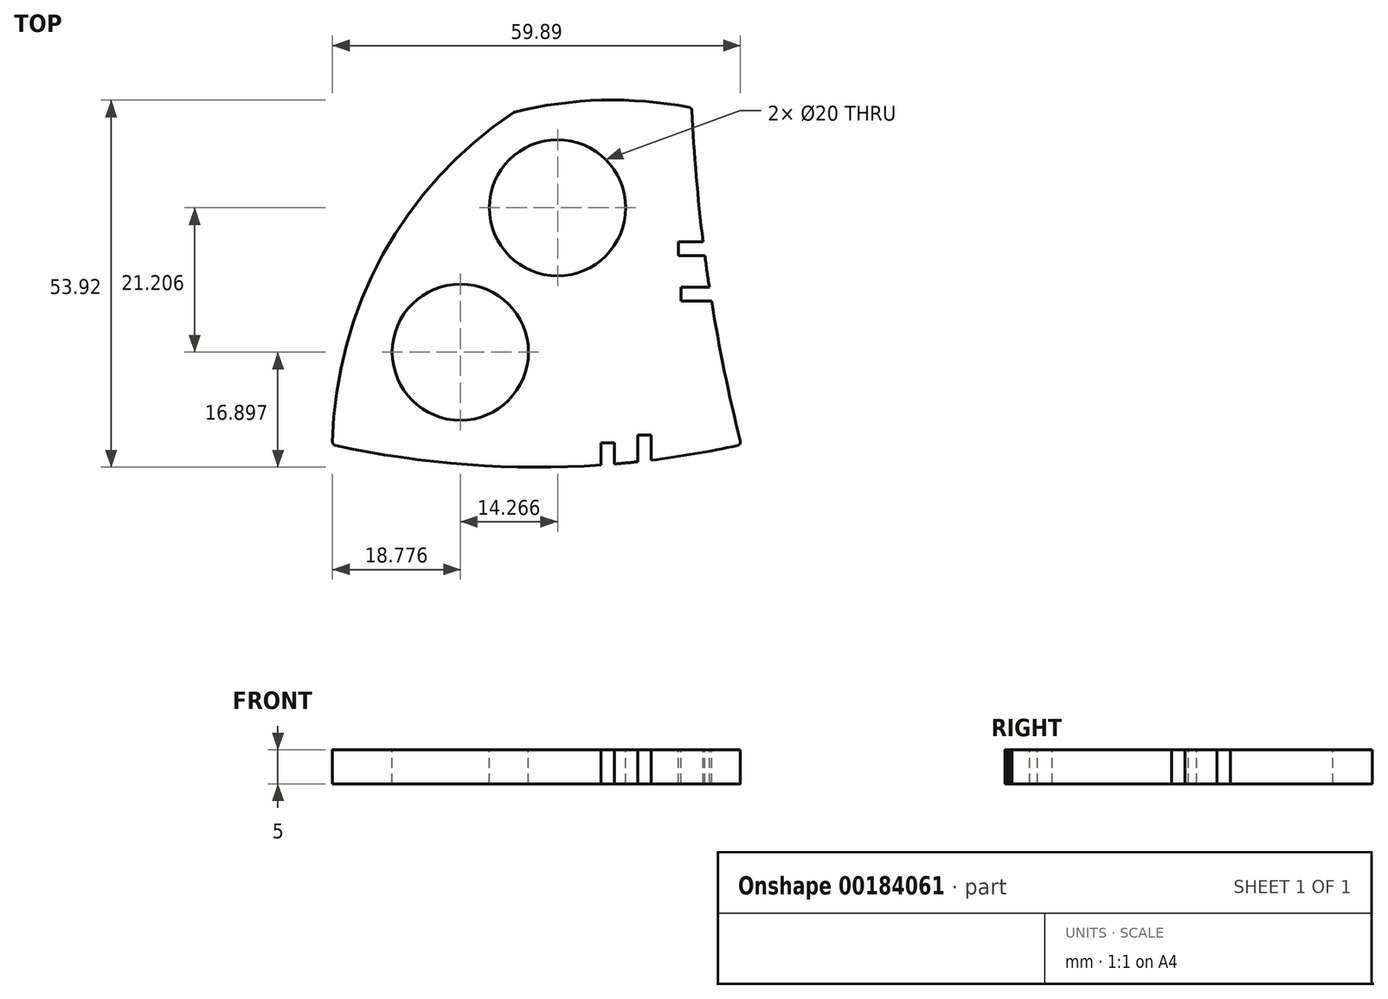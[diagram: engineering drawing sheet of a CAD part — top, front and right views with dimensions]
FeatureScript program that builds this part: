
annotation { "Feature Type Name" : "Feature", "Feature Type Description" : "" }
export const myFeature = defineFeature(function(context is Context, id is Id, definition is map)
    precondition{}
    {
        {
            var Q0;
            Q0=qCreatedBy(makeId("Top.planeOp"),FACE);
            var sketch = newSketch(context, id + "F0", { "sketchPlane" : qUnion([Q0])});
            skArc(sketch, "E0", {"start": v(-12.1, 38.1) * mm, "mid": v(-25.17, 39.22) * mm, "end": v(-38.18, 37.48) * mm});
            skArc(sketch, "E1", {"start": v(-12.1, 38.1) * mm, "mid": v(-9.74, 13.18) * mm, "end": v(-4.85, -11.37) * mm});
            skArc(sketch, "E2", {"start": v(-64.85, -11.37) * mm, "mid": v(-34.85, -14.68) * mm, "end": v(-4.85, -11.37) * mm});
            skArc(sketch, "E3", {"start": v(-38.18, 37.48) * mm, "mid": v(-57.55, 16.35) * mm, "end": v(-64.85, -11.37) * mm});
            skSolve(sketch);
        }
        {
            var Q0;
            Q0=makeQuery(id+"F0.imprint","IMPRINT",FACE,{"disambiguationData":[TD([[makeQuery(id+"F0.imprint","IMPRINT",EDGE,{"derivedFrom":sQuery(id+"F0.wireOp",EDGE,"E0")}),1.0]])]});
            extrude(context, id + "F1", {"entities" : qUnion([Q0]), "depth" : 5 * mm});
        }
        {
            var Q0;
            Q0=makeQuery(id+"F1.opExtrude","CAP_FACE",FACE,{"disambiguationData":[OSD([sQuery(id+"F0.wireOp",EDGE,"E0"),sQuery(id+"F0.wireOp",EDGE,"E1"),sQuery(id+"F0.wireOp",EDGE,"E2"),sQuery(id+"F0.wireOp",EDGE,"E3")])],"isStart":false});
            var sketch = newSketch(context, id + "F2", { "sketchPlane" : qUnion([Q0])});
            skLineSegment(sketch, "E4.bottom", {"start": v(-14.07, 18.41) * mm, "end": v(16.42, 18.41) * mm});
            skLineSegment(sketch, "E4.top", {"start": v(-14.07, 16.41) * mm, "end": v(16.42, 16.41) * mm});
            skLineSegment(sketch, "E4.left", {"start": v(-14.07, 18.41) * mm, "end": v(-14.07, 16.41) * mm});
            skLineSegment(sketch, "E4.right", {"start": v(16.42, 18.41) * mm, "end": v(16.42, 16.41) * mm});
            skLineSegment(sketch, "E5.bottom", {"start": v(-13.69, 11.74) * mm, "end": v(37.06, 11.74) * mm});
            skLineSegment(sketch, "E5.top", {"start": v(-13.69, 9.74) * mm, "end": v(37.06, 9.74) * mm});
            skLineSegment(sketch, "E5.left", {"start": v(-13.69, 11.74) * mm, "end": v(-13.69, 9.74) * mm});
            skLineSegment(sketch, "E5.right", {"start": v(37.06, 11.74) * mm, "end": v(37.06, 9.74) * mm});
            skLineSegment(sketch, "E6.bottom", {"start": v(-20.05, -21.1) * mm, "end": v(-18.05, -21.1) * mm});
            skLineSegment(sketch, "E6.top", {"start": v(-20.05, -9.93) * mm, "end": v(-18.05, -9.93) * mm});
            skLineSegment(sketch, "E6.left", {"start": v(-20.05, -21.1) * mm, "end": v(-20.05, -9.93) * mm});
            skLineSegment(sketch, "E6.right", {"start": v(-18.05, -21.1) * mm, "end": v(-18.05, -9.93) * mm});
            skLineSegment(sketch, "E7.bottom", {"start": v(-25.45, -11.08) * mm, "end": v(-23.45, -11.08) * mm});
            skLineSegment(sketch, "E7.top", {"start": v(-25.45, -26.31) * mm, "end": v(-23.45, -26.31) * mm});
            skLineSegment(sketch, "E7.left", {"start": v(-25.45, -11.08) * mm, "end": v(-25.45, -26.31) * mm});
            skLineSegment(sketch, "E7.right", {"start": v(-23.45, -11.08) * mm, "end": v(-23.45, -26.31) * mm});
            skSolve(sketch);
        }
        {
            var Q0;
            {var subQ0=sQuery(id+"F2.wireOp",EDGE,"E4.left");Q0=makeQuery(id+"F2.imprint","IMPRINT",FACE,{"disambiguationData":[TD([[makeQuery(id+"F2.imprint","IMPRINT",EDGE,{"derivedFrom":subQ0}),1.0]])]});}
            var Q1;
            {var subQ0=sQuery(id+"F2.wireOp",EDGE,"E5.left");Q1=makeQuery(id+"F2.imprint","IMPRINT",FACE,{"disambiguationData":[TD([[makeQuery(id+"F2.imprint","IMPRINT",EDGE,{"derivedFrom":subQ0}),1.0]])]});}
            var Q2;
            {var subQ0=sQuery(id+"F2.wireOp",EDGE,"E7.bottom");Q2=makeQuery(id+"F2.imprint","IMPRINT",FACE,{"disambiguationData":[TD([[makeQuery(id+"F2.imprint","IMPRINT",EDGE,{"derivedFrom":subQ0}),-1.0]])]});}
            var Q3;
            {var subQ0=sQuery(id+"F2.wireOp",EDGE,"E6.top");Q3=makeQuery(id+"F2.imprint","IMPRINT",FACE,{"disambiguationData":[TD([[makeQuery(id+"F2.imprint","IMPRINT",EDGE,{"derivedFrom":subQ0}),-1.0]])]});}
            extrude(context, id + "F3", {"entities" : qUnion([Q0, Q1, Q2, Q3]), "operationType" : NewBodyOperationType.REMOVE, "oppositeDirection" : true, "depth" : 25 * mm});
        }
        {
            var Q0;
            Q0=makeQuery(id+"F1.opExtrude","CAP_FACE",FACE,{"disambiguationData":[OSD([sQuery(id+"F0.wireOp",EDGE,"E0"),sQuery(id+"F0.wireOp",EDGE,"E1"),sQuery(id+"F0.wireOp",EDGE,"E2"),sQuery(id+"F0.wireOp",EDGE,"E3")])],"isStart":false});
            var sketch = newSketch(context, id + "F4", { "sketchPlane" : qUnion([Q0])});
            skSolve(sketch);
        }
        {
            var Q0;
            {var subQ0=sQuery(id+"F0.wireOp",EDGE,"E0");Q0=makeQuery(id+"F4.imprint","IMPRINT",FACE,{"disambiguationData":[TD([[makeQuery(id+"F4.imprint","IMPRINT",EDGE,{"derivedFrom":makeQuery(id+"F1.opExtrude","CAP_EDGE",EDGE,{"disambiguationData":[OSD([subQ0])],"isStart":false})}),1.0]])]});}
            var sketch = newSketch(context, id + "F5", { "sketchPlane" : qUnion([Q0])});
            skCircle(sketch, "E8", {"center": v(-31.8, 23.42) * mm, "radius": 10 * mm});
            skCircle(sketch, "E9", {"center": v(-46.07, 2.22) * mm, "radius": 10 * mm});
            skSolve(sketch);
        }
        {
            var Q0;
            Q0=makeQuery(id+"F5.imprint","IMPRINT",FACE,{"disambiguationData":[TD([[makeQuery(id+"F5.imprint","IMPRINT",EDGE,{"derivedFrom":sQuery(id+"F5.wireOp",EDGE,"E9")}),1.0]])]});
            var Q1;
            Q1=makeQuery(id+"F5.imprint","IMPRINT",FACE,{"disambiguationData":[TD([[makeQuery(id+"F5.imprint","IMPRINT",EDGE,{"derivedFrom":sQuery(id+"F5.wireOp",EDGE,"E8")}),1.0]])]});
            extrude(context, id + "F6", {"entities" : qUnion([Q0, Q1]), "operationType" : NewBodyOperationType.REMOVE, "oppositeDirection" : true, "depth" : 40.2 * mm});
        }
        {
            var Q0;
            Q0=makeQuery(id+"F1.opExtrude","SWEPT_EDGE",EDGE,{"disambiguationData":[OSD([sQuery(id+"F0.wireOp",EDGE,"E1"),sQuery(id+"F0.wireOp",EDGE,"E2")])]});
            var Q1;
            Q1=makeQuery(id+"F1.opExtrude","SWEPT_EDGE",EDGE,{"disambiguationData":[OSD([sQuery(id+"F0.wireOp",EDGE,"E2"),sQuery(id+"F0.wireOp",EDGE,"E3")])]});
            var Q2;
            Q2=makeQuery(id+"F1.opExtrude","SWEPT_EDGE",EDGE,{"disambiguationData":[OSD([sQuery(id+"F0.wireOp",EDGE,"E0"),sQuery(id+"F0.wireOp",EDGE,"E1")])]});
            var Q3;
            Q3=makeQuery(id+"F1.opExtrude","SWEPT_EDGE",EDGE,{"disambiguationData":[OSD([sQuery(id+"F0.wireOp",EDGE,"E0"),sQuery(id+"F0.wireOp",EDGE,"E3")])]});
            fillet(context, id + "F7", {"entities" : qUnion([Q0, Q1, Q2, Q3]), "radius" : 0.5 * mm, "tangentPropagation" : true, "allowEdgeOverflow" : false});
        }
    });
